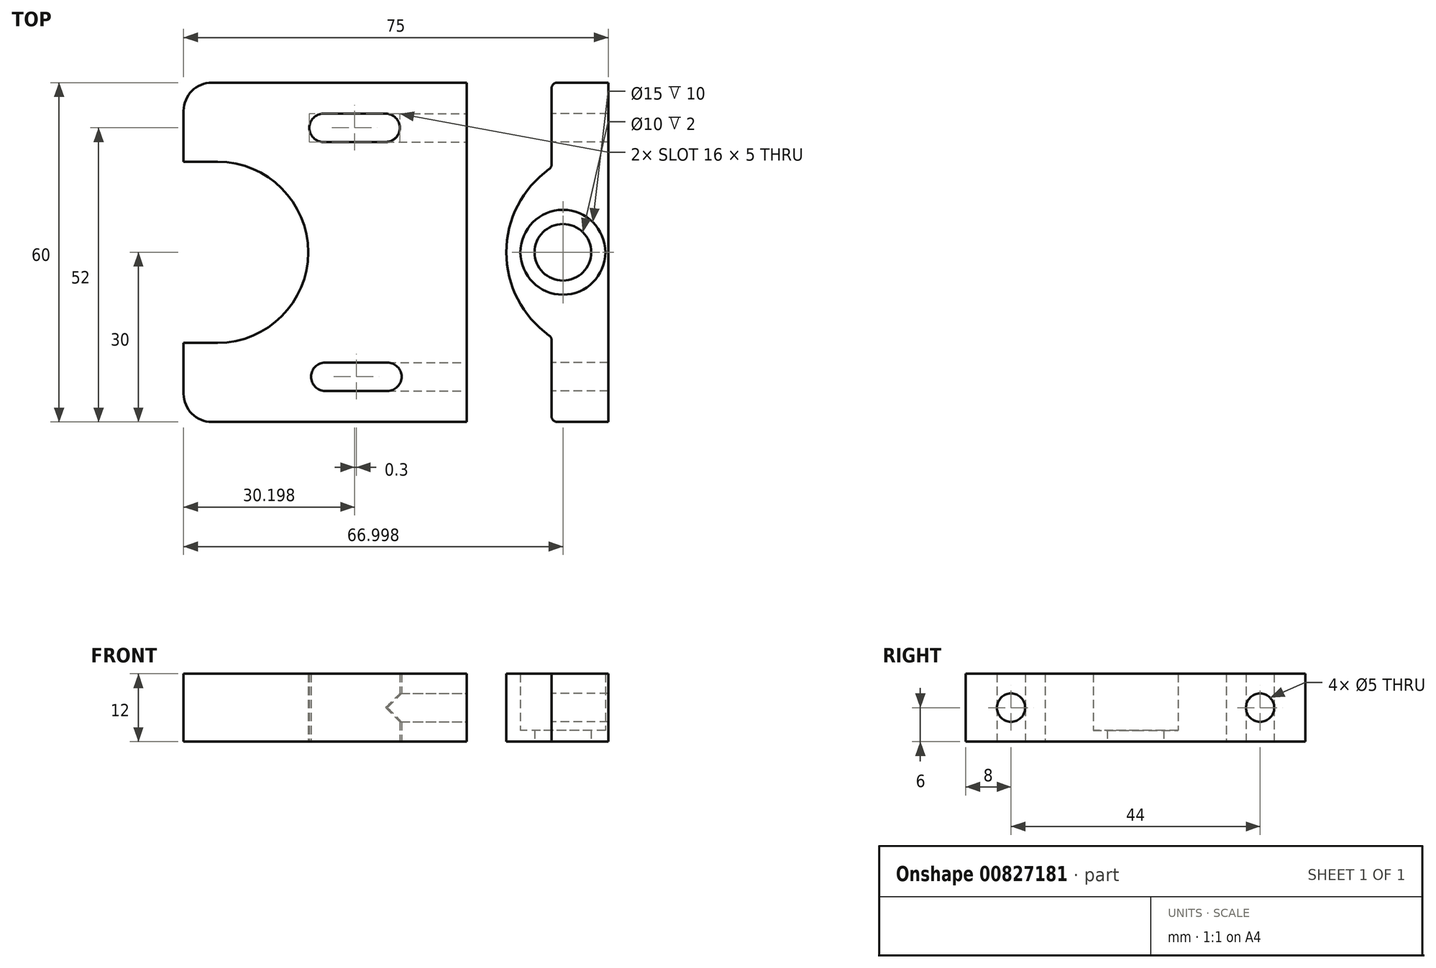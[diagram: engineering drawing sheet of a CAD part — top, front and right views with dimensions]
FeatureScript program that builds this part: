
annotation { "Feature Type Name" : "Feature", "Feature Type Description" : "" }
export const myFeature = defineFeature(function(context is Context, id is Id, definition is map)
    precondition{}
    {
        {
            var Q0;
            Q0=qCreatedBy(makeId("Top.planeOp"),FACE);
            var sketch = newSketch(context, id + "F0", { "sketchPlane" : qUnion([Q0])});
            skLineSegment(sketch, "E0.bottom", {"start": v(5.25, 143.35) * mm, "end": v(11.25, 143.35) * mm, "construction": true});
            skLineSegment(sketch, "E0.top", {"start": v(5.25, -56.65) * mm, "end": v(11.25, -56.65) * mm, "construction": true});
            skLineSegment(sketch, "E1", {"start": v(11.25, 0) * mm, "end": v(23.25, 0) * mm, "construction": true});
            skCircle(sketch, "E2", {"center": v(23.25, 0) * mm, "radius": 11 * mm, "construction": true});
            skLineSegment(sketch, "E3", {"start": v(23.25, 0) * mm, "end": v(-37.75, 0) * mm, "construction": true});
            skCircle(sketch, "E4", {"center": v(-37.75, 0) * mm, "radius": 12.5 * mm, "construction": true});
            skCircle(sketch, "E5", {"center": v(23.25, 0) * mm, "radius": 12.5 * mm, "construction": true});
            skCircle(sketch, "E6", {"center": v(-37.75, 0) * mm, "radius": 28 * mm, "construction": true});
            skLineSegment(sketch, "E7", {"start": v(6.25, 0) * mm, "end": v(6.25, 30) * mm});
            skLineSegment(sketch, "E8", {"start": v(6.25, 30) * mm, "end": v(-43.75, 30) * mm});
            skLineSegment(sketch, "E9", {"start": v(-43.75, 30) * mm, "end": v(-43.75, 16) * mm});
            skLineSegment(sketch, "E10", {"start": v(-43.75, -30) * mm, "end": v(6.25, -30) * mm});
            skLineSegment(sketch, "E11", {"start": v(6.25, -30) * mm, "end": v(6.25, 0) * mm});
            skLineSegment(sketch, "E12", {"start": v(-37.75, 16) * mm, "end": v(-43.75, 16) * mm});
            skLineSegment(sketch, "E13", {"start": v(-37.75, -16) * mm, "end": v(-43.75, -16) * mm});
            skArc(sketch, "E14.trimOffspring", {"start": v(-37.75, -16) * mm, "mid": v(-21.75, 0) * mm, "end": v(-37.75, 16) * mm});
            skLineSegment(sketch, "E15.trimOffspring", {"start": v(-43.75, -16) * mm, "end": v(-43.75, -30) * mm});
            skLineSegment(sketch, "E16", {"start": v(-37.75, -28) * mm, "end": v(6.25, -28) * mm, "construction": true});
            skLineSegment(sketch, "E17", {"start": v(-37.75, 28) * mm, "end": v(6.25, 28) * mm, "construction": true});
            skLineSegment(sketch, "E18", {"start": v(-37.75, 0) * mm, "end": v(-37.75, 16) * mm, "construction": true});
            skLineSegment(sketch, "E19", {"start": v(-37.75, 0) * mm, "end": v(-37.75, -16) * mm, "construction": true});
            skLineSegment(sketch, "E20", {"start": v(-37.75, 0) * mm, "end": v(-7.75, 0) * mm, "construction": true});
            skLineSegment(sketch, "E21", {"start": v(-7.75, 0) * mm, "end": v(-7.75, 22) * mm, "construction": true});
            skLineSegment(sketch, "E22", {"start": v(-7.75, 0) * mm, "end": v(-7.75, -22) * mm, "construction": true});
            skLineSegment(sketch, "E23", {"start": v(-7.75, 22) * mm, "end": v(-13.25, 22) * mm, "construction": true});
            skLineSegment(sketch, "E24", {"start": v(-7.75, -22) * mm, "end": v(-13.25, -22) * mm, "construction": true});
            skCircle(sketch, "E25", {"center": v(-13.25, -22) * mm, "radius": 2.5 * mm, "construction": true});
            skCircle(sketch, "E26", {"center": v(-13.25, 22) * mm, "radius": 2.5 * mm, "construction": true});
            skArc(sketch, "E27", {"start": v(-7.75, -24.5) * mm, "mid": v(-5.25, -22) * mm, "end": v(-7.75, -19.5) * mm});
            skLineSegment(sketch, "E28", {"start": v(-13.25, -22) * mm, "end": v(-18.75, -22) * mm, "construction": true});
            skArc(sketch, "E29", {"start": v(-18.75, -19.5) * mm, "mid": v(-21.25, -22) * mm, "end": v(-18.75, -24.5) * mm});
            skLineSegment(sketch, "E30", {"start": v(-18.75, -22) * mm, "end": v(-18.75, -19.5) * mm, "construction": true});
            skLineSegment(sketch, "E31", {"start": v(-18.75, -19.5) * mm, "end": v(-18.75, -24.5) * mm, "construction": true});
            skLineSegment(sketch, "E32", {"start": v(-7.75, -22) * mm, "end": v(-7.75, -24.5) * mm, "construction": true});
            skLineSegment(sketch, "E33", {"start": v(-18.75, -19.5) * mm, "end": v(-7.75, -19.5) * mm});
            skLineSegment(sketch, "E34", {"start": v(-18.75, -24.5) * mm, "end": v(-7.75, -24.5) * mm});
            skArc(sketch, "E35", {"start": v(-8.05, 19.5) * mm, "mid": v(-5.55, 22) * mm, "end": v(-8.05, 24.5) * mm});
            skArc(sketch, "E36", {"start": v(-19.05, 24.5) * mm, "mid": v(-21.55, 22) * mm, "end": v(-19.05, 19.5) * mm});
            skLineSegment(sketch, "E37", {"start": v(-19.05, 24.5) * mm, "end": v(-8.05, 24.5) * mm});
            skLineSegment(sketch, "E38", {"start": v(-19.05, 19.5) * mm, "end": v(-8.05, 19.5) * mm});
            skLineSegment(sketch, "E39", {"start": v(-13.25, 22) * mm, "end": v(31.35, 22) * mm, "construction": true});
            skLineSegment(sketch, "E40", {"start": v(-13.25, -22) * mm, "end": v(47, -22) * mm, "construction": true});
            skSolve(sketch);
        }
        {
            var Q0;
            Q0=makeQuery(id+"F0.imprint","IMPRINT",FACE,{"disambiguationData":[TD([[makeQuery(id+"F0.imprint","IMPRINT",EDGE,{"derivedFrom":sQuery(id+"F0.wireOp",EDGE,"E7")}),1.0]])]});
            extrude(context, id + "F1", {"entities" : qUnion([Q0]), "depth" : 12 * mm, "offsetDistance" : 25 * mm});
        }
        {
            var Q0;
            Q0=makeQuery(id+"F1.opExtrude","SWEPT_FACE",FACE,{"disambiguationData":[OSD([sQuery(id+"F0.wireOp",EDGE,"E7"),sQuery(id+"F0.wireOp",EDGE,"E11")])]});
            var sketch = newSketch(context, id + "F2", { "sketchPlane" : qUnion([Q0])});
            skLineSegment(sketch, "E41", {"start": v(-30, 12) * mm, "end": v(-22, 12) * mm, "construction": true});
            skLineSegment(sketch, "E42", {"start": v(-22, 12) * mm, "end": v(-22, 6) * mm, "construction": true});
            skLineSegment(sketch, "E43", {"start": v(30, 12) * mm, "end": v(22, 12) * mm, "construction": true});
            skLineSegment(sketch, "E44", {"start": v(22, 12) * mm, "end": v(22, 6) * mm, "construction": true});
            skLineSegment(sketch, "E45", {"start": v(-22, 12) * mm, "end": v(0, 12) * mm, "construction": true});
            skLineSegment(sketch, "E46", {"start": v(0, 12) * mm, "end": v(22, 12) * mm, "construction": true});
            skCircle(sketch, "E47", {"center": v(-22, 6) * mm, "radius": 2.5 * mm});
            skCircle(sketch, "E48", {"center": v(22, 6) * mm, "radius": 2.5 * mm});
            skSolve(sketch);
        }
        {
            var Q0;
            Q0=qSketchRegion(id+"F2",true);
            extrude(context, id + "F3", {"entities" : qUnion([Q0]), "operationType" : NewBodyOperationType.REMOVE, "oppositeDirection" : true, "depth" : 15 * mm, "offsetDistance" : 25 * mm});
        }
        {
            var Q0;
            Q0=makeQuery(id+"F1.opExtrude","SWEPT_EDGE",EDGE,{"disambiguationData":[OSD([sQuery(id+"F0.wireOp",EDGE,"E8"),sQuery(id+"F0.wireOp",EDGE,"E9")])]});
            var Q1;
            Q1=makeQuery(id+"F1.opExtrude","SWEPT_EDGE",EDGE,{"disambiguationData":[OSD([sQuery(id+"F0.wireOp",EDGE,"E10"),sQuery(id+"F0.wireOp",EDGE,"E15.trimOffspring")])]});
            fillet(context, id + "F4", {"entities" : qUnion([Q0, Q1]), "radius" : 5 * mm, "tangentPropagation" : true, "allowEdgeOverflow" : false});
        }
        {
            var Q0;
            Q0=qCreatedBy(makeId("Top.planeOp"),FACE);
            var sketch = newSketch(context, id + "F5", { "sketchPlane" : qUnion([Q0])});
            skLineSegment(sketch, "E49.bottom", {"start": v(12.25, 30) * mm, "end": v(31.25, 30) * mm});
            skLineSegment(sketch, "E49.top", {"start": v(12.25, -30) * mm, "end": v(31.25, -30) * mm});
            skLineSegment(sketch, "E49.left", {"start": v(6.25, 30) * mm, "end": v(6.25, -30) * mm});
            skLineSegment(sketch, "E50", {"start": v(31.25, 30) * mm, "end": v(31.25, 15) * mm});
            skLineSegment(sketch, "E51", {"start": v(31.25, -30) * mm, "end": v(31.25, -15) * mm});
            skLineSegment(sketch, "E52", {"start": v(6.25, 0) * mm, "end": v(23.25, 0) * mm, "construction": true});
            skCircle(sketch, "E53", {"center": v(23.25, 0) * mm, "radius": 7.5 * mm});
            skCircle(sketch, "E54", {"center": v(23.25, 0) * mm, "radius": 5 * mm});
            skLineSegment(sketch, "E55", {"start": v(31.25, 15) * mm, "end": v(31.25, -15) * mm});
            skLineSegment(sketch, "E56", {"start": v(31.25, 30) * mm, "end": v(21.25, 30) * mm});
            skLineSegment(sketch, "E57", {"start": v(21.25, 30) * mm, "end": v(21.25, 15) * mm});
            skLineSegment(sketch, "E58", {"start": v(31.25, -30) * mm, "end": v(21.25, -30) * mm});
            skLineSegment(sketch, "E59", {"start": v(21.25, -30) * mm, "end": v(21.25, -15) * mm});
            skLineSegment(sketch, "E60", {"start": v(31.25, 0) * mm, "end": v(13.25, 0) * mm, "construction": true});
            skArc(sketch, "E61", {"start": v(21.25, 15) * mm, "mid": v(13.25, 0) * mm, "end": v(21.25, -15) * mm});
            skSolve(sketch);
        }
        {
            var Q0;
            Q0=makeQuery(id+"F5.imprint","IMPRINT",FACE,{"disambiguationData":[TD([[makeQuery(id+"F5.imprint","IMPRINT",EDGE,{"derivedFrom":sQuery(id+"F5.wireOp",EDGE,"E50")}),-1.0]])]});
            extrude(context, id + "F6", {"entities" : qUnion([Q0]), "operationType" : NewBodyOperationType.ADD, "depth" : 12 * mm, "offsetDistance" : 25 * mm});
        }
        {
            var Q0;
            Q0=makeQuery(id+"F5.imprint","IMPRINT",FACE,{"disambiguationData":[TD([[makeQuery(id+"F5.imprint","IMPRINT",EDGE,{"derivedFrom":sQuery(id+"F5.wireOp",EDGE,"E53")}),1.0]])]});
            extrude(context, id + "F7", {"entities" : qUnion([Q0]), "operationType" : NewBodyOperationType.ADD, "depth" : 2 * mm, "offsetDistance" : 25 * mm});
        }
        {
            var Q0;
            Q0=qSketchRegion(id+"F2",true);
            var Q1;
            Q1=makeQuery(id+"F6.opExtrude","SWEPT_FACE",FACE,{"disambiguationData":[OSD([sQuery(id+"F5.wireOp",EDGE,"E50")])]});
            extrude(context, id + "F8", {"entities" : qUnion([Q0, Q1]), "operationType" : NewBodyOperationType.REMOVE, "depth" : 25 * mm, "offsetDistance" : 25 * mm});
        }
        {
            var Q0;
            Q0=makeQuery(id+"F6.opExtrude","SWEPT_EDGE",EDGE,{"disambiguationData":[OSD([sQuery(id+"F5.wireOp",EDGE,"E56"),sQuery(id+"F5.wireOp",EDGE,"E57")])]});
            var Q1;
            Q1=makeQuery(id+"F6.opExtrude","SWEPT_EDGE",EDGE,{"disambiguationData":[OSD([sQuery(id+"F5.wireOp",EDGE,"E57"),sQuery(id+"F5.wireOp",EDGE,"E61")])]});
            var Q2;
            Q2=makeQuery(id+"F6.opExtrude","SWEPT_EDGE",EDGE,{"disambiguationData":[OSD([sQuery(id+"F5.wireOp",EDGE,"E59"),sQuery(id+"F5.wireOp",EDGE,"E61")])]});
            var Q3;
            Q3=makeQuery(id+"F6.opExtrude","SWEPT_EDGE",EDGE,{"disambiguationData":[OSD([sQuery(id+"F5.wireOp",EDGE,"E58"),sQuery(id+"F5.wireOp",EDGE,"E59")])]});
            fillet(context, id + "F9", {"entities" : qUnion([Q0, Q1, Q2, Q3]), "radius" : 1 * mm, "tangentPropagation" : true, "allowEdgeOverflow" : false});
        }
    });
